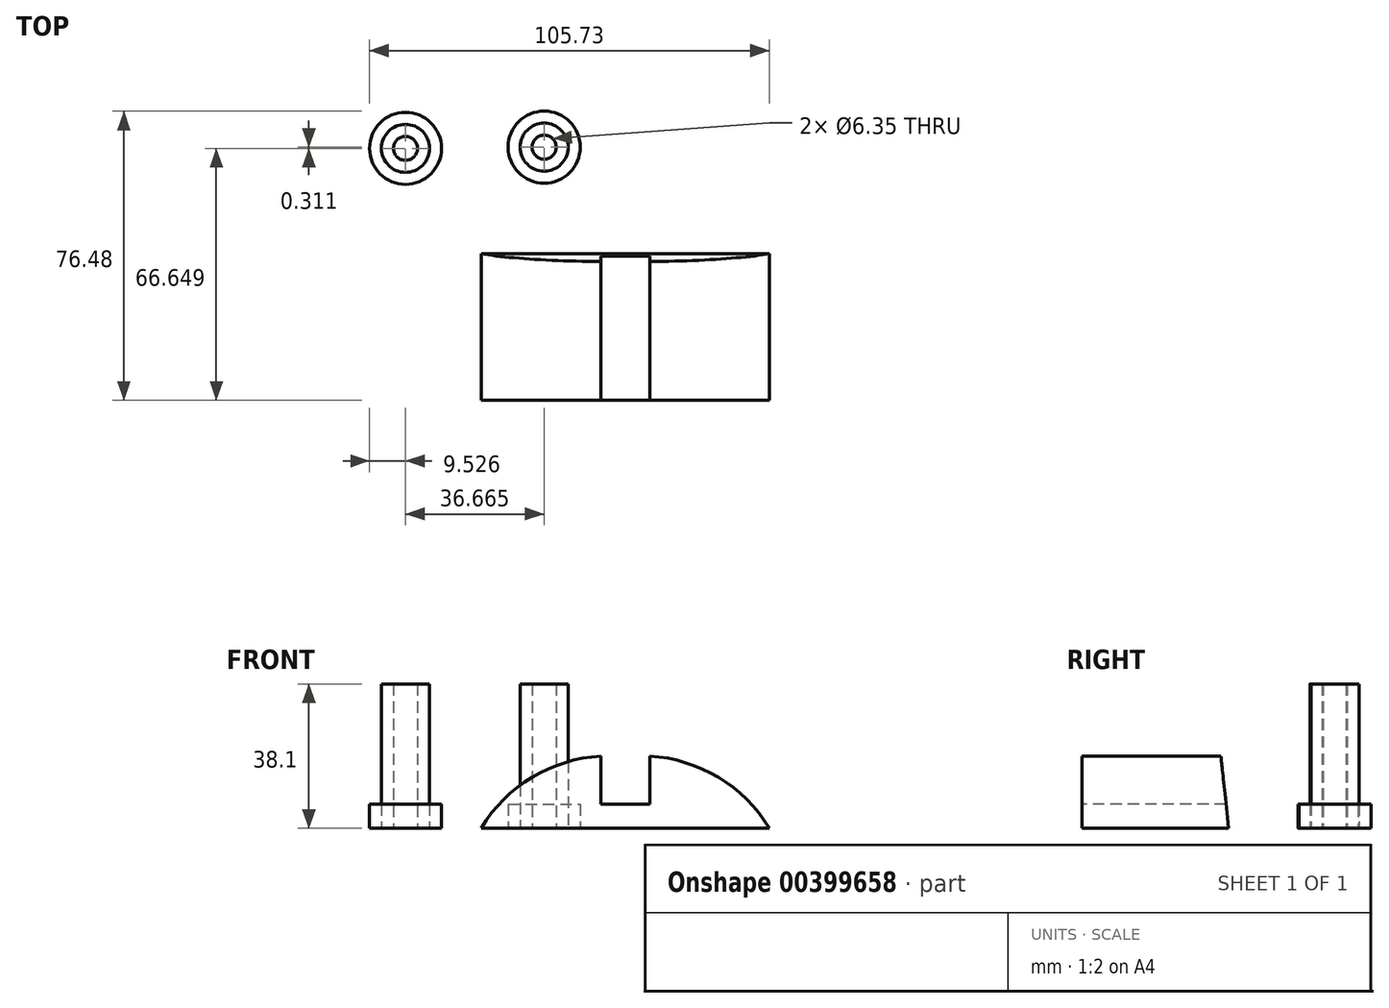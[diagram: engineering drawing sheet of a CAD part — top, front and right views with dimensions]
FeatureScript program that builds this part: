
annotation { "Feature Type Name" : "Feature", "Feature Type Description" : "" }
export const myFeature = defineFeature(function(context is Context, id is Id, definition is map)
    precondition{}
    {
        {
            var Q0;
            Q0=qCreatedBy(makeId("Right.planeOp"),FACE);
            var sketch = newSketch(context, id + "F0", { "sketchPlane" : qUnion([Q0])});
            skLineSegment(sketch, "E0", {"start": v(101.38, -204.07) * mm, "end": v(51.64, 19.05) * mm});
            skLineSegment(sketch, "E1", {"start": v(51.64, 19.05) * mm, "end": v(0, 19.05) * mm});
            skLineSegment(sketch, "E2", {"start": v(0, 19.05) * mm, "end": v(0, 25.4) * mm});
            skLineSegment(sketch, "E3", {"start": v(0, 25.4) * mm, "end": v(-12.7, 25.4) * mm});
            skLineSegment(sketch, "E4", {"start": v(-12.7, 25.4) * mm, "end": v(-12.7, 6.35) * mm});
            skLineSegment(sketch, "E5", {"start": v(-12.7, 6.35) * mm, "end": v(38.1, 6.35) * mm});
            skLineSegment(sketch, "E6", {"start": v(38.1, 6.35) * mm, "end": v(60.74, -204.07) * mm});
            skLineSegment(sketch, "E7", {"start": v(60.74, -204.07) * mm, "end": v(101.38, -204.07) * mm});
            skCircle(sketch, "E8", {"center": v(58.53, -70.72) * mm, "radius": 6.48 * mm});
            skCircle(sketch, "E9", {"center": v(73.2, -159.62) * mm, "radius": 6.48 * mm});
            skSolve(sketch);
        }
        {
            var Q0;
            Q0=qCreatedBy(makeId("Front.planeOp"),FACE);
            var sketch = newSketch(context, id + "F1", { "sketchPlane" : qUnion([Q0])});
            skLineSegment(sketch, "E10", {"start": v(0, 0) * mm, "end": v(38.1, 0) * mm});
            skArc(sketch, "E11", {"start": v(38.1, 0) * mm, "mid": v(24.64, 13.42) * mm, "end": v(6.48, 19.05) * mm});
            skLineSegment(sketch, "E12", {"start": v(6.48, 19.05) * mm, "end": v(6.48, 6.35) * mm});
            skLineSegment(sketch, "E13", {"start": v(6.48, 6.35) * mm, "end": v(0, 6.35) * mm});
            skLineSegment(sketch, "E14", {"start": v(0, 6.35) * mm, "end": v(0, 0) * mm});
            skLineSegment(sketch, "E15.MirrorCS", {"start": v(-6.48, 19.05) * mm, "end": v(-6.48, 6.35) * mm});
            skArc(sketch, "E16.MirrorCS", {"start": v(-38.1, 0) * mm, "mid": v(-24.64, 13.42) * mm, "end": v(-6.48, 19.05) * mm});
            skLineSegment(sketch, "E17", {"start": v(-38.1, 0) * mm, "end": v(0, 0) * mm});
            skLineSegment(sketch, "E18", {"start": v(-6.48, 6.35) * mm, "end": v(0, 6.35) * mm});
            skSolve(sketch);
        }
        {
            var Q0;
            Q0=sQuery(id+"F0.wireOp",EDGE,"E6");
            cPlane(context, id + "F2", {"entities" : qUnion([Q0]), "cplaneType" : CPlaneType.LINE_ANGLE, "offset" : 25.4 * mm, "angle" : 90 * degree, "width" : 152.4 * mm, "height" : 152.4 * mm});
        }
        {
            var Q0;
            Q0=makeQuery(id+"F1.imprint","IMPRINT",FACE,{"disambiguationData":[TD([[makeQuery(id+"F1.imprint","IMPRINT",EDGE,{"derivedFrom":sQuery(id+"F1.wireOp",EDGE,"E10")}),1.0]])]});
            var Q1;
            Q1=makeQuery(id+"F1.imprint","IMPRINT",FACE,{"disambiguationData":[TD([[makeQuery(id+"F1.imprint","IMPRINT",EDGE,{"derivedFrom":sQuery(id+"F1.wireOp",EDGE,"E14")}),-1.0]])]});
            var Q2;
            Q2=qCreatedBy(id+"F2.planeOp",FACE);
            extrude(context, id + "F3", {"entities" : qUnion([Q0, Q1]), "endBound" : BoundingType.UP_TO_SURFACE, "oppositeDirection" : true, "endBoundEntityFace" : qUnion([Q2]), "depth" : 25.4 * mm});
        }
        {
            var Q0;
            Q0=qCreatedBy(makeId("Top.planeOp"),FACE);
            var sketch = newSketch(context, id + "F4", { "sketchPlane" : qUnion([Q0])});
            skCircle(sketch, "E19", {"center": v(-58.1, 66.65) * mm, "radius": 3.18 * mm});
            skCircle(sketch, "E20", {"center": v(-21.44, 66.96) * mm, "radius": 3.18 * mm});
            skCircle(sketch, "E21", {"center": v(-58.1, 66.65) * mm, "radius": 6.35 * mm});
            skCircle(sketch, "E22", {"center": v(-21.44, 66.96) * mm, "radius": 6.35 * mm});
            skSolve(sketch);
        }
        {
            var Q0;
            Q0 = qSketchRegion(id + "F4", true);
            extrude(context, id + "F5", {"entities" : qUnion([Q0]), "depth" : 38.1 * mm});
        }
        {
            var Q0;
            Q0=makeQuery(id+"F5.opExtrude","CAP_FACE",FACE,{"disambiguationData":[OSD([sQuery(id+"F4.wireOp",EDGE,"E19"),sQuery(id+"F4.wireOp",EDGE,"E21")])],"isStart":true});
            var sketch = newSketch(context, id + "F6", { "sketchPlane" : qUnion([Q0])});
            skCircle(sketch, "E23", {"center": v(-58.1, -66.65) * mm, "radius": 9.53 * mm});
            skCircle(sketch, "E24", {"center": v(-21.44, -66.96) * mm, "radius": 9.53 * mm});
            skSolve(sketch);
        }
        {
            var Q0;
            Q0 = qSketchRegion(id + "F6", true);
            extrude(context, id + "F7", {"entities" : qUnion([Q0]), "oppositeDirection" : true, "depth" : 6.35 * mm});
        }
    });
